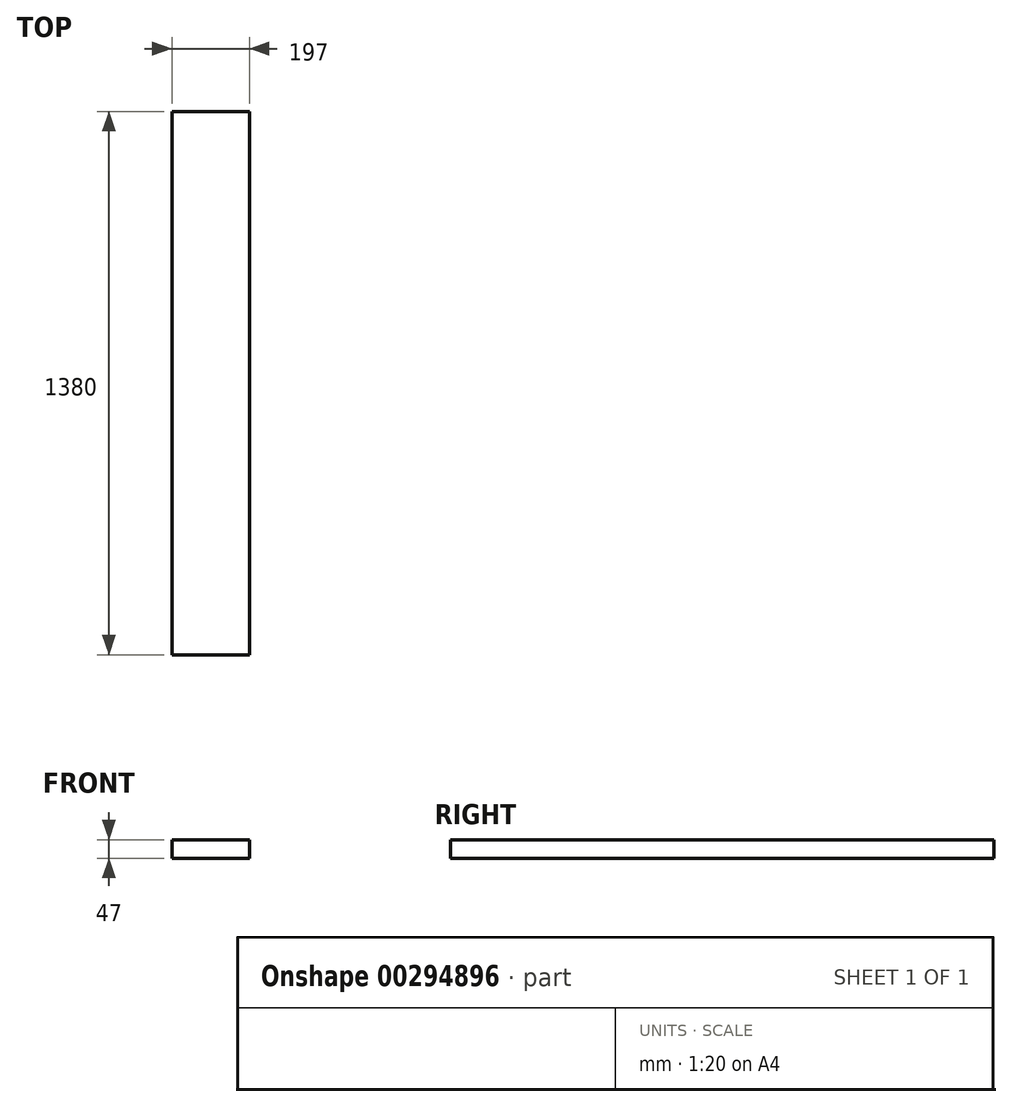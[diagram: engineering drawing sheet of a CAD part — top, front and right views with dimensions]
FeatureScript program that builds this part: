
annotation { "Feature Type Name" : "Feature", "Feature Type Description" : "" }
export const myFeature = defineFeature(function(context is Context, id is Id, definition is map)
    precondition{}
    {
        {
            var Q0;
            Q0=qCreatedBy(makeId("Front.planeOp"),FACE);
            var sketch = newSketch(context, id + "F0", { "sketchPlane" : qUnion([Q0])});
            skLineSegment(sketch, "E0.bottom", {"start": v(98.5, 23.5) * mm, "end": v(-98.5, 23.5) * mm});
            skLineSegment(sketch, "E0.top", {"start": v(98.5, -23.5) * mm, "end": v(-98.5, -23.5) * mm});
            skLineSegment(sketch, "E0.left", {"start": v(98.5, 23.5) * mm, "end": v(98.5, -23.5) * mm});
            skLineSegment(sketch, "E0.right", {"start": v(-98.5, 23.5) * mm, "end": v(-98.5, -23.5) * mm});
            skPoint(sketch, "E0.middle", {"position": v(0, 0) * mm});
            skSolve(sketch);
        }
        {
            var Q0;
            Q0 = qSketchRegion(id + "F0", true);
            extrude(context, id + "F1", {"entities" : qUnion([Q0]), "depth" : 1380 * mm});
        }
    });
